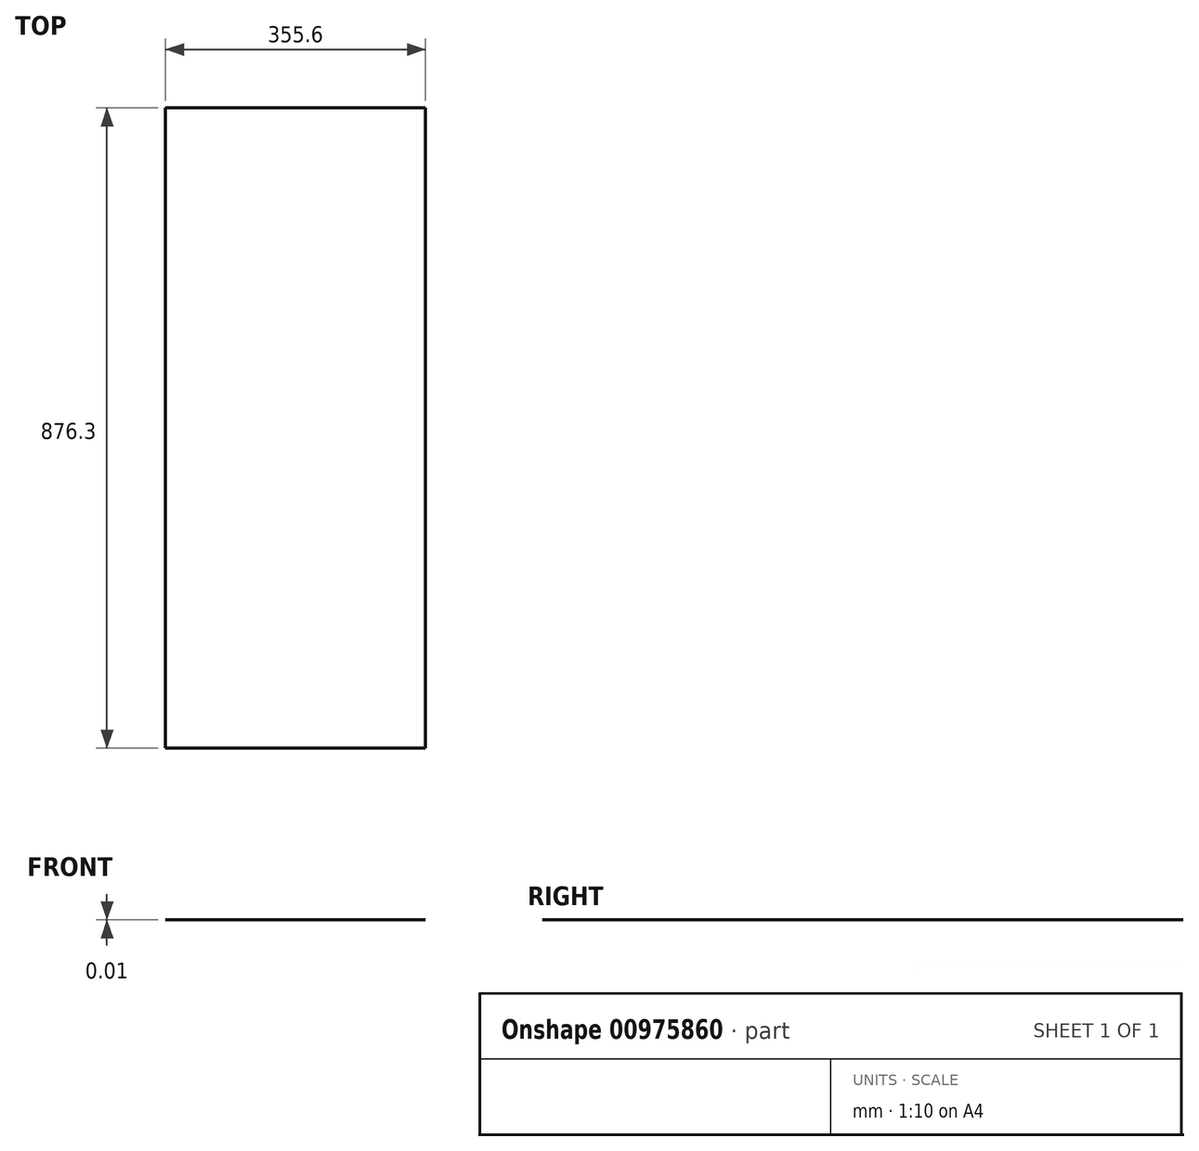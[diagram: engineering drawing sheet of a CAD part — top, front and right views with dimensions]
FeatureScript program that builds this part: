
annotation { "Feature Type Name" : "Feature", "Feature Type Description" : "" }
export const myFeature = defineFeature(function(context is Context, id is Id, definition is map)
    precondition{}
    {
        {
            var Q0;
            Q0=qCreatedBy(makeId("Top.planeOp"),FACE);
            var sketch = newSketch(context, id + "F0", { "sketchPlane" : qUnion([Q0])});
            skLineSegment(sketch, "E0.bottom", {"start": v(0, 0) * mm, "end": v(355.6, 0) * mm});
            skLineSegment(sketch, "E0.top", {"start": v(0, 876.3) * mm, "end": v(355.6, 876.3) * mm});
            skLineSegment(sketch, "E0.left", {"start": v(0, 0) * mm, "end": v(0, 876.3) * mm});
            skLineSegment(sketch, "E0.right", {"start": v(355.6, 0) * mm, "end": v(355.6, 876.3) * mm});
            skSolve(sketch);
        }
        {
            var Q0;
            Q0=makeQuery(id+"F0.imprint","IMPRINT",FACE,{"disambiguationData":[TD([[makeQuery(id+"F0.imprint","IMPRINT",EDGE,{"derivedFrom":sQuery(id+"F0.wireOp",EDGE,"E0.bottom")}),1.0]])]});
            extrude(context, id + "F1", {"entities" : qUnion([Q0]), "depth" : 3 / 203.2 * mm, "offsetDistance" : 25.4 * mm});
        }
    });
